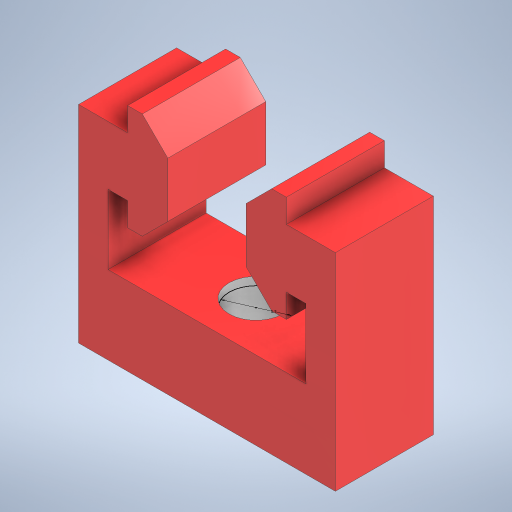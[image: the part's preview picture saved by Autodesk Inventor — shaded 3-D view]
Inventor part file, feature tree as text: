
AUTODESK INVENTOR PART (.ipt)
format: ipt  version: 2023.2 (Build 272271030, 271C)  size: 294,912 bytes
history: native  units: mm
features: extrude x2, sketch x2, plane x1
ambient origin geometry x8: Origin, YZ Plane, XZ Plane, XY Plane, X Axis, Y Axis, Z Axis, Center Point
bodies: Solid1 (feature_tree)
feature tree (5):
  extrude  "Extrusion1"  Depth=3.0mm
  plane  "Work Plane1"
  sketch  "Sketch2"  dims[d14=0.1mm d17=0.1mm d18=0.09mm d19=10.0mm d20=0.0mm d21=-7.8mm d22=5.5mm d27=0.0mm d28=0.0mm d31=8.0mm]
  extrude  "Extrusion3"  Depth=8.0mm
  sketch  "Sketch1"  dims[d0=20.0mm d1=20.0mm d2=5.0mm d3=6.1mm d4=6.1mm d5=1.5mm d6=4.5mm d7=4.5mm d8=1.5mm d9=6.9mm d10=1.8mm d13=3.0mm]
